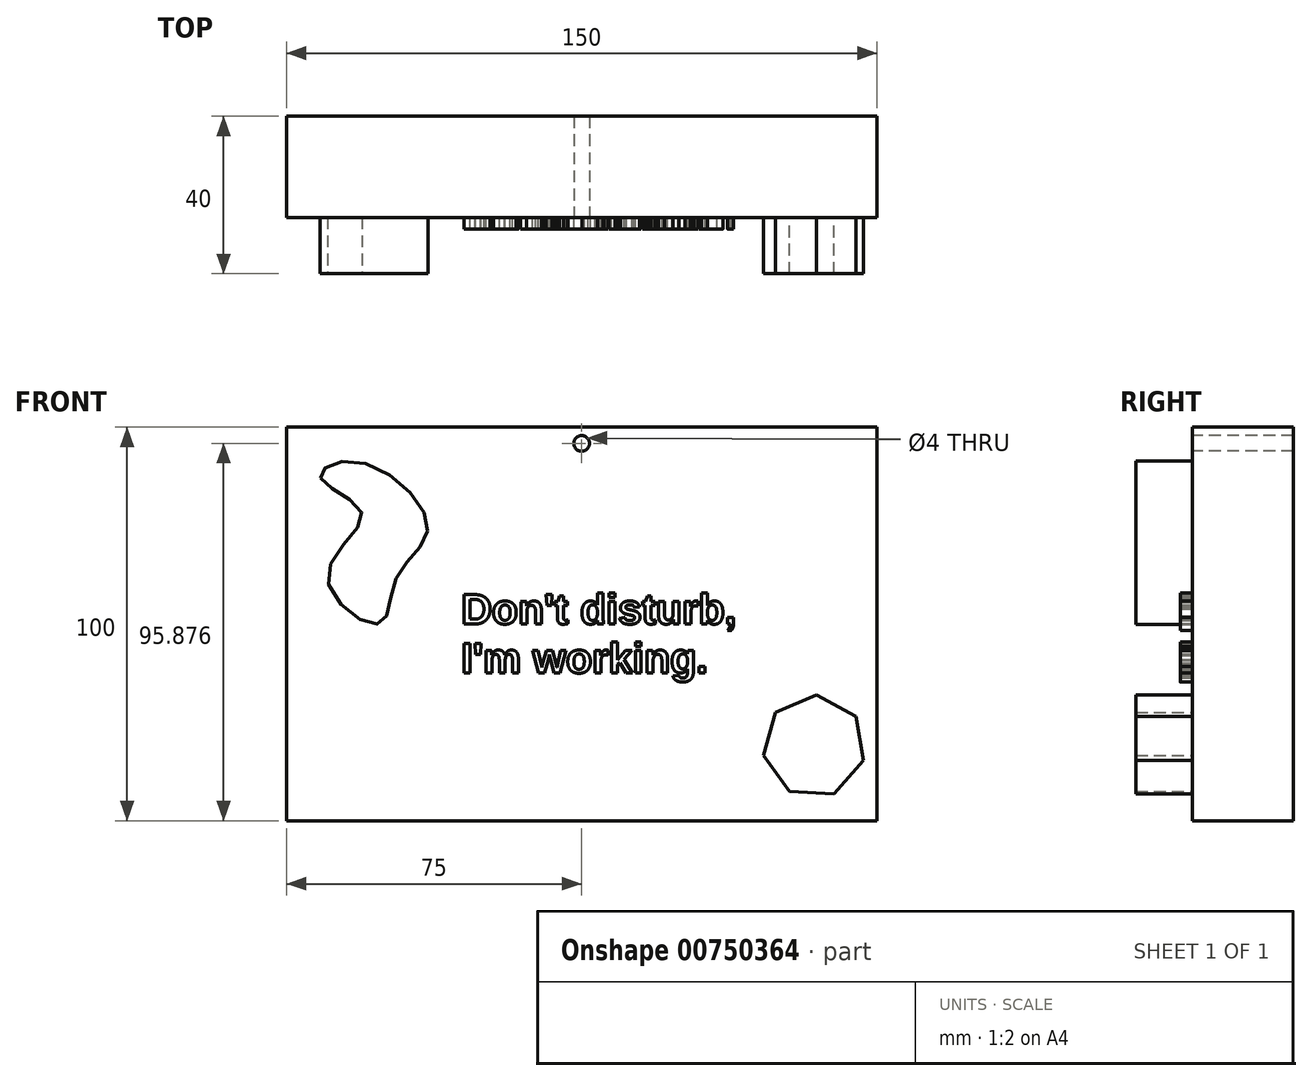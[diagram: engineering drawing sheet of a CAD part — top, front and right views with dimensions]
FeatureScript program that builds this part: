
annotation { "Feature Type Name" : "Feature", "Feature Type Description" : "" }
export const myFeature = defineFeature(function(context is Context, id is Id, definition is map)
    precondition{}
    {
        {
            var Q0;
            Q0=qCreatedBy(makeId("Front.planeOp"),FACE);
            var sketch = newSketch(context, id + "F0", { "sketchPlane" : qUnion([Q0])});
            skLineSegment(sketch, "E0.bottom", {"start": v(75, -50) * mm, "end": v(-75, -50) * mm});
            skLineSegment(sketch, "E0.top", {"start": v(75, 50) * mm, "end": v(-75, 50) * mm});
            skLineSegment(sketch, "E0.left", {"start": v(75, -50) * mm, "end": v(75, 50) * mm});
            skLineSegment(sketch, "E0.right", {"start": v(-75, -50) * mm, "end": v(-75, 50) * mm});
            skPoint(sketch, "E0.middle", {"position": v(0, 0) * mm});
            skSolve(sketch);
        }
        {
            var Q0;
            Q0 = qSketchRegion(id + "F0", true);
            extrude(context, id + "F1", {"entities" : qUnion([Q0]), "depth" : 0.7 * mm, "offsetDistance" : 25 * mm});
        }
        {
            var Q0;
            Q0=qCreatedBy(makeId("Front.planeOp"),FACE);
            var sketch = newSketch(context, id + "F2", { "sketchPlane" : qUnion([Q0])});
            skFitSpline(sketch, "E1", {"points": [v(-66.35, 37.04) * mm, v(-55.85, 28.1) * mm, v(-64.57, 12) * mm, v(-51.6, 0) * mm, v(-47.13, 11.56) * mm, v(-39.09, 24.75) * mm, v(-57.2, 41.29) * mm, v(-66.35, 37.04) * mm]});
            skCircle(sketch, "E2.cCircle", {"center": v(59.03, -31.13) * mm, "radius": 11.77 * mm, "construction": true});
            skLineSegment(sketch, "E2.0", {"start": v(49.23, -22.49) * mm, "end": v(46.17, -33.4) * mm});
            skLineSegment(sketch, "E2.1", {"start": v(59.68, -18.08) * mm, "end": v(49.23, -22.49) * mm});
            skLineSegment(sketch, "E2.2", {"start": v(69.64, -23.5) * mm, "end": v(59.68, -18.08) * mm});
            skLineSegment(sketch, "E2.3", {"start": v(71.61, -34.67) * mm, "end": v(69.64, -23.5) * mm});
            skLineSegment(sketch, "E2.4", {"start": v(64.11, -43.17) * mm, "end": v(71.61, -34.67) * mm});
            skLineSegment(sketch, "E2.5", {"start": v(52.79, -42.6) * mm, "end": v(64.11, -43.17) * mm});
            skLineSegment(sketch, "E2.6", {"start": v(46.17, -33.4) * mm, "end": v(52.79, -42.6) * mm});
            skPoint(sketch, "E2.0.midPoint", {"position": v(47.7, -27.95) * mm});
            skSolve(sketch);
        }
        {
            var Q0;
            Q0=makeQuery(id+"F1.opExtrude","CAP_FACE",FACE,{"disambiguationData":[OSD([sQuery(id+"F0.wireOp",EDGE,"E0.bottom"),sQuery(id+"F0.wireOp",EDGE,"E0.top"),sQuery(id+"F0.wireOp",EDGE,"E0.left"),sQuery(id+"F0.wireOp",EDGE,"E0.right")])],"isStart":false});
            extrude(context, id + "F3", {"entities" : qUnion([Q0]), "operationType" : NewBodyOperationType.ADD, "depth" : 25 * mm, "offsetDistance" : 25 * mm});
        }
        {
            var Q0;
            Q0 = qSketchRegion(id + "F2", true);
            extrude(context, id + "F4", {"entities" : qUnion([Q0]), "operationType" : NewBodyOperationType.ADD, "depth" : 40 * mm, "offsetDistance" : 25 * mm});
        }
        {
            var Q0;
            Q0=makeQuery(id+"F3.opExtrude","CAP_FACE",FACE,{"disambiguationData":[OSD([sQuery(id+"F0.wireOp",EDGE,"E0.bottom"),sQuery(id+"F0.wireOp",EDGE,"E0.top"),sQuery(id+"F0.wireOp",EDGE,"E0.left"),sQuery(id+"F0.wireOp",EDGE,"E0.right")])],"isStart":false});
            var sketch = newSketch(context, id + "F5", { "sketchPlane" : qUnion([Q0])});
            skText(sketch, "E3", { "text": "Don\'t disturb,\nI\'m working.", "fontName": "Arimo-Bold.ttf"});
            const initialGuessF5  = {"E3": [-0.03063, 0, 1, 0, 0.0078]};
            skSetInitialGuess(sketch, initialGuessF5);
            skSolve(sketch);
        }
        {
            var Q0;
            Q0 = qSketchRegion(id + "F5", true);
            extrude(context, id + "F6", {"entities" : qUnion([Q0]), "operationType" : NewBodyOperationType.ADD, "depth" : 3 * mm, "offsetDistance" : 25 * mm});
        }
        {
            var Q0;
            {var subQ0=sQuery(id+"F0.wireOp",EDGE,"E0.top");var subQ1=sQuery(id+"F0.wireOp",EDGE,"E0.bottom");var subQ2=sQuery(id+"F0.wireOp",EDGE,"E0.right");var subQ3=sQuery(id+"F0.wireOp",EDGE,"E0.left");Q0=makeQuery(id+"F6.boolean.opBoolean","SPLIT",FACE,{"disambiguationData":[TD([makeQuery(id+"F1.opExtrude","SWEPT_FACE",FACE,{"disambiguationData":[OSD([subQ1])]})])],"derivedFrom":makeQuery(id+"F3.opExtrude","CAP_FACE",FACE,{"disambiguationData":[OSD([subQ1,subQ0,subQ3,subQ2])],"isStart":false})});}
            var sketch = newSketch(context, id + "F7", { "sketchPlane" : qUnion([Q0])});
            skCircle(sketch, "E4", {"center": v(0, 45.88) * mm, "radius": 2 * mm});
            skSolve(sketch);
        }
        {
            var Q0;
            Q0 = qSketchRegion(id + "F7", true);
            extrude(context, id + "F8", {"entities" : qUnion([Q0]), "operationType" : NewBodyOperationType.REMOVE, "endBound" : BoundingType.UP_TO_NEXT, "oppositeDirection" : true, "depth" : 25 * mm, "offsetDistance" : 25 * mm});
        }
    });
